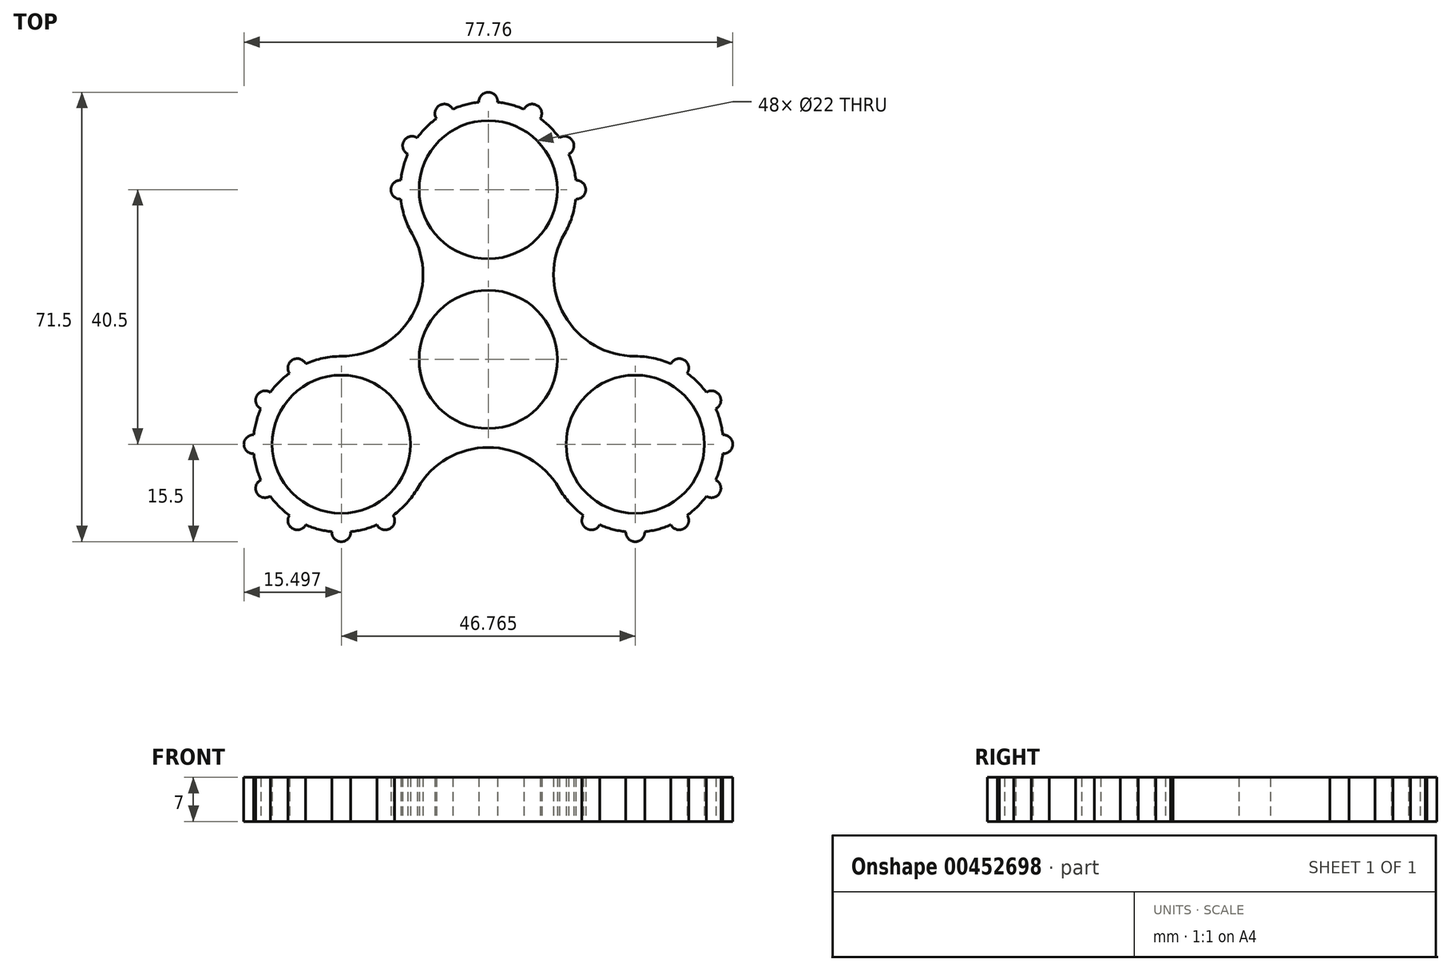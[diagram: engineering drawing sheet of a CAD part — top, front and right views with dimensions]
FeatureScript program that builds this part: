
annotation { "Feature Type Name" : "Feature", "Feature Type Description" : "" }
export const myFeature = defineFeature(function(context is Context, id is Id, definition is map)
    precondition{}
    {
        {
            var Q0;
            Q0=qCreatedBy(makeId("Top.planeOp"),FACE);
            var sketch = newSketch(context, id + "F0", { "sketchPlane" : qUnion([Q0])});
            skCircle(sketch, "E0", {"center": v(0, 0) * mm, "radius": 11 * mm});
            skLineSegment(sketch, "E1", {"start": v(0, 0) * mm, "end": v(0, 27) * mm});
            skCircle(sketch, "E2.0", {"center": v(0, 0) * mm, "radius": 14 * mm});
            skCircle(sketch, "E3", {"center": v(0, 27) * mm, "radius": 11 * mm});
            skCircle(sketch, "E4.0", {"center": v(0, 27) * mm, "radius": 14 * mm});
            skLineSegment(sketch, "E5", {"start": v(0, 27) * mm, "end": v(-14, 27) * mm});
            skArc(sketch, "E6", {"start": v(-13.92, 28.5) * mm, "mid": v(-15.5, 27) * mm, "end": v(-13.92, 25.5) * mm});
            skArc(sketch, "E7.1.0", {"start": v(-11.3, 35.26) * mm, "mid": v(-13.42, 34.75) * mm, "end": v(-12.8, 32.66) * mm});
            skArc(sketch, "E7.2.0", {"start": v(-5.66, 39.8) * mm, "mid": v(-7.75, 40.42) * mm, "end": v(-8.26, 38.3) * mm});
            skArc(sketch, "E7.3.0", {"start": v(1.5, 40.92) * mm, "mid": v(0, 42.5) * mm, "end": v(-1.5, 40.92) * mm});
            skArc(sketch, "E7.4.0", {"start": v(8.26, 38.3) * mm, "mid": v(7.75, 40.42) * mm, "end": v(5.66, 39.8) * mm});
            skArc(sketch, "E7.5.0", {"start": v(12.8, 32.66) * mm, "mid": v(13.42, 34.75) * mm, "end": v(11.3, 35.26) * mm});
            skArc(sketch, "E7.6.0", {"start": v(13.92, 25.5) * mm, "mid": v(15.5, 27) * mm, "end": v(13.92, 28.5) * mm});
            skLineSegment(sketch, "E7.anchor1", {"start": v(0, 27) * mm, "end": v(-13.92, 25.5) * mm, "construction": true});
            skLineSegment(sketch, "E7.anchor2", {"start": v(0, 27) * mm, "end": v(13.92, 28.5) * mm, "construction": true});
            skCircle(sketch, "E8.1.0", {"center": v(-23.38, -13.5) * mm, "radius": 14 * mm});
            skCircle(sketch, "E8.1.1", {"center": v(-23.38, -13.5) * mm, "radius": 11 * mm});
            skArc(sketch, "E8.1.2", {"start": v(-17.72, -26.3) * mm, "mid": v(-15.63, -26.92) * mm, "end": v(-15.13, -24.8) * mm});
            skArc(sketch, "E8.1.3", {"start": v(-24.88, -27.42) * mm, "mid": v(-23.38, -29) * mm, "end": v(-21.88, -27.42) * mm});
            skArc(sketch, "E8.1.4", {"start": v(-31.64, -24.8) * mm, "mid": v(-31.13, -26.92) * mm, "end": v(-29.05, -26.3) * mm});
            skArc(sketch, "E8.1.5", {"start": v(-36.19, -19.16) * mm, "mid": v(-36.8, -21.25) * mm, "end": v(-34.69, -21.76) * mm});
            skArc(sketch, "E8.1.6", {"start": v(-37.3, -12) * mm, "mid": v(-38.88, -13.5) * mm, "end": v(-37.3, -15) * mm});
            skArc(sketch, "E8.1.7", {"start": v(-34.69, -5.24) * mm, "mid": v(-36.8, -5.75) * mm, "end": v(-36.19, -7.84) * mm});
            skArc(sketch, "E8.1.8", {"start": v(-29.05, -0.7) * mm, "mid": v(-31.13, -0.08) * mm, "end": v(-31.64, -2.2) * mm});
            skCircle(sketch, "E8.2.0", {"center": v(23.38, -13.5) * mm, "radius": 14 * mm});
            skCircle(sketch, "E8.2.1", {"center": v(23.38, -13.5) * mm, "radius": 11 * mm});
            skArc(sketch, "E8.2.2", {"start": v(31.64, -2.2) * mm, "mid": v(31.13, -0.08) * mm, "end": v(29.05, -0.7) * mm});
            skArc(sketch, "E8.2.3", {"start": v(36.19, -7.84) * mm, "mid": v(36.8, -5.75) * mm, "end": v(34.69, -5.24) * mm});
            skArc(sketch, "E8.2.4", {"start": v(37.3, -15) * mm, "mid": v(38.88, -13.5) * mm, "end": v(37.3, -12) * mm});
            skArc(sketch, "E8.2.5", {"start": v(34.69, -21.76) * mm, "mid": v(36.8, -21.25) * mm, "end": v(36.19, -19.16) * mm});
            skArc(sketch, "E8.2.6", {"start": v(29.05, -26.3) * mm, "mid": v(31.13, -26.92) * mm, "end": v(31.64, -24.8) * mm});
            skArc(sketch, "E8.2.7", {"start": v(21.88, -27.42) * mm, "mid": v(23.38, -29) * mm, "end": v(24.88, -27.42) * mm});
            skArc(sketch, "E8.2.8", {"start": v(15.13, -24.8) * mm, "mid": v(15.63, -26.92) * mm, "end": v(17.72, -26.3) * mm});
            skLineSegment(sketch, "E9", {"start": v(0, 27) * mm, "end": v(-12.12, 34) * mm});
            skLineSegment(sketch, "E10.MirrorCS", {"start": v(0, 27) * mm, "end": v(-12.12, 20) * mm});
            skLineSegment(sketch, "E11.MirrorCS", {"start": v(0, 27) * mm, "end": v(12.12, 20) * mm});
            skLineSegment(sketch, "E12.1.0", {"start": v(-23.38, -13.5) * mm, "end": v(-11.26, -20.5) * mm});
            skLineSegment(sketch, "E12.1.1", {"start": v(-23.38, -13.5) * mm, "end": v(-23.38, 0.5) * mm});
            skLineSegment(sketch, "E12.2.0", {"start": v(23.38, -13.5) * mm, "end": v(23.38, 0.5) * mm});
            skLineSegment(sketch, "E12.2.1", {"start": v(23.38, -13.5) * mm, "end": v(11.26, -20.5) * mm});
            skLineSegment(sketch, "E13", {"start": v(0, 0) * mm, "end": v(-12.12, 7) * mm});
            skArc(sketch, "E14", {"start": v(-23.38, 0.5) * mm, "mid": v(-12.12, 7) * mm, "end": v(-12.12, 20) * mm});
            skArc(sketch, "E15.1.0", {"start": v(11.26, -20.5) * mm, "mid": v(0, -14) * mm, "end": v(-11.26, -20.5) * mm});
            skArc(sketch, "E15.2.0", {"start": v(12.12, 20) * mm, "mid": v(12.12, 7) * mm, "end": v(23.38, 0.5) * mm});
            skSolve(sketch);
        }
        {
            var Q0;
            {var subQ0=sQuery(id+"F0.wireOp",EDGE,"E5");var subQ5=sQuery(id+"F0.wireOp",EDGE,"E3");var subQ6=makeQuery(id+"F0.imprint","INTERSECT",VERTEX,{"derivedFrom":[subQ5,subQ0]});Q0=makeQuery(id+"F0.imprint","IMPRINT",FACE,{"disambiguationData":[TD([[makeQuery(id+"F0.imprint","IMPRINT",EDGE,{"disambiguationData":[TD([[subQ6,1.0]])],"derivedFrom":subQ5}),-1.0]])]});}
            var Q1;
            {var subQ11=sQuery(id+"F0.wireOp",EDGE,"E9");var subQ12=sQuery(id+"F0.wireOp",EDGE,"E3");var subQ13=makeQuery(id+"F0.imprint","INTERSECT",VERTEX,{"derivedFrom":[subQ12,subQ11]});Q1=makeQuery(id+"F0.imprint","IMPRINT",FACE,{"disambiguationData":[TD([[makeQuery(id+"F0.imprint","IMPRINT",EDGE,{"disambiguationData":[TD([[subQ13,1.0]])],"derivedFrom":subQ12}),-1.0]])]});}
            var Q2;
            {var subQ0=sQuery(id+"F0.wireOp",EDGE,"E7.1.0");Q2=makeQuery(id+"F0.imprint","IMPRINT",FACE,{"disambiguationData":[TD([[makeQuery(id+"F0.imprint","IMPRINT",EDGE,{"derivedFrom":subQ0}),1.0]])]});}
            var Q3;
            {var subQ0=sQuery(id+"F0.wireOp",EDGE,"E7.2.0");Q3=makeQuery(id+"F0.imprint","IMPRINT",FACE,{"disambiguationData":[TD([[makeQuery(id+"F0.imprint","IMPRINT",EDGE,{"derivedFrom":subQ0}),1.0]])]});}
            var Q4;
            {var subQ0=sQuery(id+"F0.wireOp",EDGE,"E7.3.0");Q4=makeQuery(id+"F0.imprint","IMPRINT",FACE,{"disambiguationData":[TD([[makeQuery(id+"F0.imprint","IMPRINT",EDGE,{"derivedFrom":subQ0}),1.0]])]});}
            var Q5;
            {var subQ0=sQuery(id+"F0.wireOp",EDGE,"E7.4.0");Q5=makeQuery(id+"F0.imprint","IMPRINT",FACE,{"disambiguationData":[TD([[makeQuery(id+"F0.imprint","IMPRINT",EDGE,{"derivedFrom":subQ0}),1.0]])]});}
            var Q6;
            {var subQ0=sQuery(id+"F0.wireOp",EDGE,"E7.5.0");Q6=makeQuery(id+"F0.imprint","IMPRINT",FACE,{"disambiguationData":[TD([[makeQuery(id+"F0.imprint","IMPRINT",EDGE,{"derivedFrom":subQ0}),1.0]])]});}
            var Q7;
            {var subQ0=sQuery(id+"F0.wireOp",EDGE,"E7.6.0");Q7=makeQuery(id+"F0.imprint","IMPRINT",FACE,{"disambiguationData":[TD([[makeQuery(id+"F0.imprint","IMPRINT",EDGE,{"derivedFrom":subQ0}),1.0]])]});}
            var Q8;
            {var subQ0=sQuery(id+"F0.wireOp",EDGE,"E2.0");var subQ1=sQuery(id+"F0.wireOp",EDGE,"E1");var subQ2=makeQuery(id+"F0.imprint","INTERSECT",VERTEX,{"derivedFrom":[subQ1,subQ0]});Q8=makeQuery(id+"F0.imprint","IMPRINT",FACE,{"disambiguationData":[TD([[makeQuery(id+"F0.imprint","IMPRINT",EDGE,{"disambiguationData":[TD([[subQ2,-1.0]])],"derivedFrom":subQ1}),-1.0]])]});}
            var Q9;
            {var subQ0=sQuery(id+"F0.wireOp",EDGE,"E4.0");var subQ1=sQuery(id+"F0.wireOp",EDGE,"E1");var subQ2=makeQuery(id+"F0.imprint","INTERSECT",VERTEX,{"derivedFrom":[subQ1,subQ0]});Q9=makeQuery(id+"F0.imprint","IMPRINT",FACE,{"disambiguationData":[TD([[makeQuery(id+"F0.imprint","IMPRINT",EDGE,{"disambiguationData":[TD([[subQ2,-1.0]])],"derivedFrom":subQ1}),1.0]])]});}
            var Q10;
            {var subQ0=sQuery(id+"F0.wireOp",EDGE,"E4.0");var subQ1=sQuery(id+"F0.wireOp",EDGE,"E1");var subQ2=makeQuery(id+"F0.imprint","INTERSECT",VERTEX,{"derivedFrom":[subQ1,subQ0]});Q10=makeQuery(id+"F0.imprint","IMPRINT",FACE,{"disambiguationData":[TD([[makeQuery(id+"F0.imprint","IMPRINT",EDGE,{"disambiguationData":[TD([[subQ2,-1.0]])],"derivedFrom":subQ1}),-1.0]])]});}
            var Q11;
            {var subQ3=sQuery(id+"F0.wireOp",EDGE,"E2.0");var subQ6=sQuery(id+"F0.wireOp",EDGE,"E1");var subQ9=makeQuery(id+"F0.imprint","INTERSECT",VERTEX,{"derivedFrom":[subQ6,subQ3]});Q11=makeQuery(id+"F0.imprint","IMPRINT",FACE,{"disambiguationData":[TD([[makeQuery(id+"F0.imprint","IMPRINT",EDGE,{"disambiguationData":[TD([[subQ9,-1.0]])],"derivedFrom":subQ6}),1.0]])]});}
            var Q12;
            {var subQ2=sQuery(id+"F0.wireOp",EDGE,"E6");Q12=makeQuery(id+"F0.imprint","IMPRINT",FACE,{"disambiguationData":[TD([[makeQuery(id+"F0.imprint","IMPRINT",EDGE,{"derivedFrom":subQ2}),1.0]])]});}
            var Q13;
            {var subQ1=sQuery(id+"F0.wireOp",EDGE,"E2.0");var subQ3=sQuery(id+"F0.wireOp",EDGE,"E4.0");var subQ4=makeQuery(id+"F0.imprint","INTERSECT",VERTEX,{"disambiguationData":[OD(1.0)],"derivedFrom":[subQ1,subQ3]});Q13=makeQuery(id+"F0.imprint","IMPRINT",FACE,{"disambiguationData":[TD([[makeQuery(id+"F0.imprint","IMPRINT",EDGE,{"disambiguationData":[TD([[subQ4,-1.0]])],"derivedFrom":subQ1}),-1.0]])]});}
            var Q14;
            {var subQ1=sQuery(id+"F0.wireOp",EDGE,"E1");var subQ5=sQuery(id+"F0.wireOp",EDGE,"E0");var subQ6=makeQuery(id+"F0.imprint","INTERSECT",VERTEX,{"derivedFrom":[subQ5,subQ1]});Q14=makeQuery(id+"F0.imprint","IMPRINT",FACE,{"disambiguationData":[TD([[makeQuery(id+"F0.imprint","IMPRINT",EDGE,{"disambiguationData":[TD([[subQ6,-1.0]])],"derivedFrom":subQ5}),-1.0]])]});}
            var Q15;
            {var subQ1=sQuery(id+"F0.wireOp",EDGE,"E1");var subQ9=sQuery(id+"F0.wireOp",EDGE,"E0");var subQ10=makeQuery(id+"F0.imprint","INTERSECT",VERTEX,{"derivedFrom":[subQ9,subQ1]});Q15=makeQuery(id+"F0.imprint","IMPRINT",FACE,{"disambiguationData":[TD([[makeQuery(id+"F0.imprint","IMPRINT",EDGE,{"disambiguationData":[TD([[subQ10,1.0]])],"derivedFrom":subQ9}),-1.0]])]});}
            var Q16;
            {var subQ0=sQuery(id+"F0.wireOp",EDGE,"E15.2.0");var subQ1=sQuery(id+"F0.wireOp",EDGE,"E2.0");var subQ2=makeQuery(id+"F0.imprint","INTERSECT",VERTEX,{"derivedFrom":[subQ1,subQ0]});Q16=makeQuery(id+"F0.imprint","IMPRINT",FACE,{"disambiguationData":[TD([[makeQuery(id+"F0.imprint","IMPRINT",EDGE,{"disambiguationData":[TD([[subQ2,-1.0]])],"derivedFrom":subQ1}),-1.0]])]});}
            var Q17;
            {var subQ0=sQuery(id+"F0.wireOp",EDGE,"E15.2.0");var subQ1=sQuery(id+"F0.wireOp",EDGE,"E2.0");var subQ2=makeQuery(id+"F0.imprint","INTERSECT",VERTEX,{"derivedFrom":[subQ1,subQ0]});Q17=makeQuery(id+"F0.imprint","IMPRINT",FACE,{"disambiguationData":[TD([[makeQuery(id+"F0.imprint","IMPRINT",EDGE,{"disambiguationData":[TD([[subQ2,1.0]])],"derivedFrom":subQ1}),-1.0]])]});}
            var Q18;
            {var subQ0=sQuery(id+"F0.wireOp",EDGE,"E8.2.0");var subQ1=sQuery(id+"F0.wireOp",EDGE,"E2.0");var subQ2=makeQuery(id+"F0.imprint","INTERSECT",VERTEX,{"disambiguationData":[OD(0.0)],"derivedFrom":[subQ1,subQ0]});Q18=makeQuery(id+"F0.imprint","IMPRINT",FACE,{"disambiguationData":[TD([[makeQuery(id+"F0.imprint","IMPRINT",EDGE,{"disambiguationData":[TD([[subQ2,-1.0]])],"derivedFrom":subQ1}),1.0]])]});}
            var Q19;
            {var subQ1=sQuery(id+"F0.wireOp",EDGE,"E8.2.0");var subQ3=sQuery(id+"F0.wireOp",EDGE,"E2.0");var subQ4=makeQuery(id+"F0.imprint","INTERSECT",VERTEX,{"disambiguationData":[OD(0.0)],"derivedFrom":[subQ3,subQ1]});Q19=makeQuery(id+"F0.imprint","IMPRINT",FACE,{"disambiguationData":[TD([[makeQuery(id+"F0.imprint","IMPRINT",EDGE,{"disambiguationData":[TD([[subQ4,-1.0]])],"derivedFrom":subQ3}),-1.0]])]});}
            var Q20;
            {var subQ1=sQuery(id+"F0.wireOp",EDGE,"E8.2.0");var subQ12=sQuery(id+"F0.wireOp",EDGE,"E8.2.7");var subQ13=makeQuery(id+"F0.imprint","INTERSECT",VERTEX,{"disambiguationData":[OD(0.0)],"derivedFrom":[subQ1,subQ12]});Q20=makeQuery(id+"F0.imprint","IMPRINT",FACE,{"disambiguationData":[TD([[makeQuery(id+"F0.imprint","IMPRINT",EDGE,{"disambiguationData":[TD([[subQ13,1.0]])],"derivedFrom":subQ1}),1.0]])]});}
            var Q21;
            {var subQ0=sQuery(id+"F0.wireOp",EDGE,"E8.2.2");Q21=makeQuery(id+"F0.imprint","IMPRINT",FACE,{"disambiguationData":[TD([[makeQuery(id+"F0.imprint","IMPRINT",EDGE,{"derivedFrom":subQ0}),1.0]])]});}
            var Q22;
            {var subQ0=sQuery(id+"F0.wireOp",EDGE,"E8.2.3");Q22=makeQuery(id+"F0.imprint","IMPRINT",FACE,{"disambiguationData":[TD([[makeQuery(id+"F0.imprint","IMPRINT",EDGE,{"derivedFrom":subQ0}),1.0]])]});}
            var Q23;
            {var subQ0=sQuery(id+"F0.wireOp",EDGE,"E8.2.4");Q23=makeQuery(id+"F0.imprint","IMPRINT",FACE,{"disambiguationData":[TD([[makeQuery(id+"F0.imprint","IMPRINT",EDGE,{"derivedFrom":subQ0}),1.0]])]});}
            var Q24;
            {var subQ0=sQuery(id+"F0.wireOp",EDGE,"E8.2.5");Q24=makeQuery(id+"F0.imprint","IMPRINT",FACE,{"disambiguationData":[TD([[makeQuery(id+"F0.imprint","IMPRINT",EDGE,{"derivedFrom":subQ0}),1.0]])]});}
            var Q25;
            {var subQ0=sQuery(id+"F0.wireOp",EDGE,"E8.2.6");Q25=makeQuery(id+"F0.imprint","IMPRINT",FACE,{"disambiguationData":[TD([[makeQuery(id+"F0.imprint","IMPRINT",EDGE,{"derivedFrom":subQ0}),1.0]])]});}
            var Q26;
            {var subQ0=sQuery(id+"F0.wireOp",EDGE,"E8.2.7");Q26=makeQuery(id+"F0.imprint","IMPRINT",FACE,{"disambiguationData":[TD([[makeQuery(id+"F0.imprint","IMPRINT",EDGE,{"derivedFrom":subQ0}),1.0]])]});}
            var Q27;
            {var subQ0=sQuery(id+"F0.wireOp",EDGE,"E8.2.8");Q27=makeQuery(id+"F0.imprint","IMPRINT",FACE,{"disambiguationData":[TD([[makeQuery(id+"F0.imprint","IMPRINT",EDGE,{"derivedFrom":subQ0}),1.0]])]});}
            var Q28;
            {var subQ0=sQuery(id+"F0.wireOp",EDGE,"E15.1.0");var subQ1=sQuery(id+"F0.wireOp",EDGE,"E2.0");var subQ2=makeQuery(id+"F0.imprint","INTERSECT",VERTEX,{"derivedFrom":[subQ1,subQ0]});Q28=makeQuery(id+"F0.imprint","IMPRINT",FACE,{"disambiguationData":[TD([[makeQuery(id+"F0.imprint","IMPRINT",EDGE,{"disambiguationData":[TD([[subQ2,-1.0]])],"derivedFrom":subQ1}),-1.0]])]});}
            var Q29;
            {var subQ0=sQuery(id+"F0.wireOp",EDGE,"E15.1.0");var subQ1=sQuery(id+"F0.wireOp",EDGE,"E2.0");var subQ2=makeQuery(id+"F0.imprint","INTERSECT",VERTEX,{"derivedFrom":[subQ1,subQ0]});Q29=makeQuery(id+"F0.imprint","IMPRINT",FACE,{"disambiguationData":[TD([[makeQuery(id+"F0.imprint","IMPRINT",EDGE,{"disambiguationData":[TD([[subQ2,1.0]])],"derivedFrom":subQ1}),-1.0]])]});}
            var Q30;
            {var subQ0=sQuery(id+"F0.wireOp",EDGE,"E8.1.0");var subQ1=sQuery(id+"F0.wireOp",EDGE,"E2.0");var subQ2=makeQuery(id+"F0.imprint","INTERSECT",VERTEX,{"disambiguationData":[OD(0.0)],"derivedFrom":[subQ1,subQ0]});Q30=makeQuery(id+"F0.imprint","IMPRINT",FACE,{"disambiguationData":[TD([[makeQuery(id+"F0.imprint","IMPRINT",EDGE,{"disambiguationData":[TD([[subQ2,-1.0]])],"derivedFrom":subQ1}),1.0]])]});}
            var Q31;
            {var subQ1=sQuery(id+"F0.wireOp",EDGE,"E2.0");var subQ3=sQuery(id+"F0.wireOp",EDGE,"E8.1.0");var subQ4=makeQuery(id+"F0.imprint","INTERSECT",VERTEX,{"disambiguationData":[OD(0.0)],"derivedFrom":[subQ1,subQ3]});Q31=makeQuery(id+"F0.imprint","IMPRINT",FACE,{"disambiguationData":[TD([[makeQuery(id+"F0.imprint","IMPRINT",EDGE,{"disambiguationData":[TD([[subQ4,1.0]])],"derivedFrom":subQ1}),-1.0]])]});}
            var Q32;
            {var subQ5=sQuery(id+"F0.wireOp",EDGE,"E8.1.0");var subQ7=sQuery(id+"F0.wireOp",EDGE,"E2.0");var subQ10=makeQuery(id+"F0.imprint","INTERSECT",VERTEX,{"disambiguationData":[OD(0.0)],"derivedFrom":[subQ7,subQ5]});Q32=makeQuery(id+"F0.imprint","IMPRINT",FACE,{"disambiguationData":[TD([[makeQuery(id+"F0.imprint","IMPRINT",EDGE,{"disambiguationData":[TD([[subQ10,-1.0]])],"derivedFrom":subQ7}),-1.0]])]});}
            var Q33;
            {var subQ1=sQuery(id+"F0.wireOp",EDGE,"E8.1.0");var subQ12=sQuery(id+"F0.wireOp",EDGE,"E8.1.7");var subQ13=makeQuery(id+"F0.imprint","INTERSECT",VERTEX,{"disambiguationData":[OD(0.0)],"derivedFrom":[subQ1,subQ12]});Q33=makeQuery(id+"F0.imprint","IMPRINT",FACE,{"disambiguationData":[TD([[makeQuery(id+"F0.imprint","IMPRINT",EDGE,{"disambiguationData":[TD([[subQ13,1.0]])],"derivedFrom":subQ1}),1.0]])]});}
            var Q34;
            {var subQ0=sQuery(id+"F0.wireOp",EDGE,"E8.1.8");Q34=makeQuery(id+"F0.imprint","IMPRINT",FACE,{"disambiguationData":[TD([[makeQuery(id+"F0.imprint","IMPRINT",EDGE,{"derivedFrom":subQ0}),1.0]])]});}
            var Q35;
            {var subQ0=sQuery(id+"F0.wireOp",EDGE,"E8.1.7");Q35=makeQuery(id+"F0.imprint","IMPRINT",FACE,{"disambiguationData":[TD([[makeQuery(id+"F0.imprint","IMPRINT",EDGE,{"derivedFrom":subQ0}),1.0]])]});}
            var Q36;
            {var subQ0=sQuery(id+"F0.wireOp",EDGE,"E8.1.6");Q36=makeQuery(id+"F0.imprint","IMPRINT",FACE,{"disambiguationData":[TD([[makeQuery(id+"F0.imprint","IMPRINT",EDGE,{"derivedFrom":subQ0}),1.0]])]});}
            var Q37;
            {var subQ0=sQuery(id+"F0.wireOp",EDGE,"E8.1.5");Q37=makeQuery(id+"F0.imprint","IMPRINT",FACE,{"disambiguationData":[TD([[makeQuery(id+"F0.imprint","IMPRINT",EDGE,{"derivedFrom":subQ0}),1.0]])]});}
            var Q38;
            {var subQ0=sQuery(id+"F0.wireOp",EDGE,"E8.1.4");Q38=makeQuery(id+"F0.imprint","IMPRINT",FACE,{"disambiguationData":[TD([[makeQuery(id+"F0.imprint","IMPRINT",EDGE,{"derivedFrom":subQ0}),1.0]])]});}
            var Q39;
            {var subQ0=sQuery(id+"F0.wireOp",EDGE,"E8.1.3");Q39=makeQuery(id+"F0.imprint","IMPRINT",FACE,{"disambiguationData":[TD([[makeQuery(id+"F0.imprint","IMPRINT",EDGE,{"derivedFrom":subQ0}),1.0]])]});}
            var Q40;
            {var subQ0=sQuery(id+"F0.wireOp",EDGE,"E8.1.2");Q40=makeQuery(id+"F0.imprint","IMPRINT",FACE,{"disambiguationData":[TD([[makeQuery(id+"F0.imprint","IMPRINT",EDGE,{"derivedFrom":subQ0}),1.0]])]});}
            var Q41;
            {var subQ0=sQuery(id+"F0.wireOp",EDGE,"E5");var subQ3=sQuery(id+"F0.wireOp",EDGE,"E3");var subQ4=makeQuery(id+"F0.imprint","INTERSECT",VERTEX,{"derivedFrom":[subQ3,subQ0]});Q41=makeQuery(id+"F0.imprint","IMPRINT",FACE,{"disambiguationData":[TD([[makeQuery(id+"F0.imprint","IMPRINT",EDGE,{"disambiguationData":[TD([[subQ4,-1.0]])],"derivedFrom":subQ3}),-1.0]])]});}
            extrude(context, id + "F1", {"entities" : qUnion([Q0, Q1, Q2, Q3, Q4, Q5, Q6, Q7, Q8, Q9, Q10, Q11, Q12, Q13, Q14, Q15, Q16, Q17, Q18, Q19, Q20, Q21, Q22, Q23, Q24, Q25, Q26, Q27, Q28, Q29, Q30, Q31, Q32, Q33, Q34, Q35, Q36, Q37, Q38, Q39, Q40, Q41]), "endBound" : BoundingType.SYMMETRIC, "depth" : 7 * mm});
        }
    });
